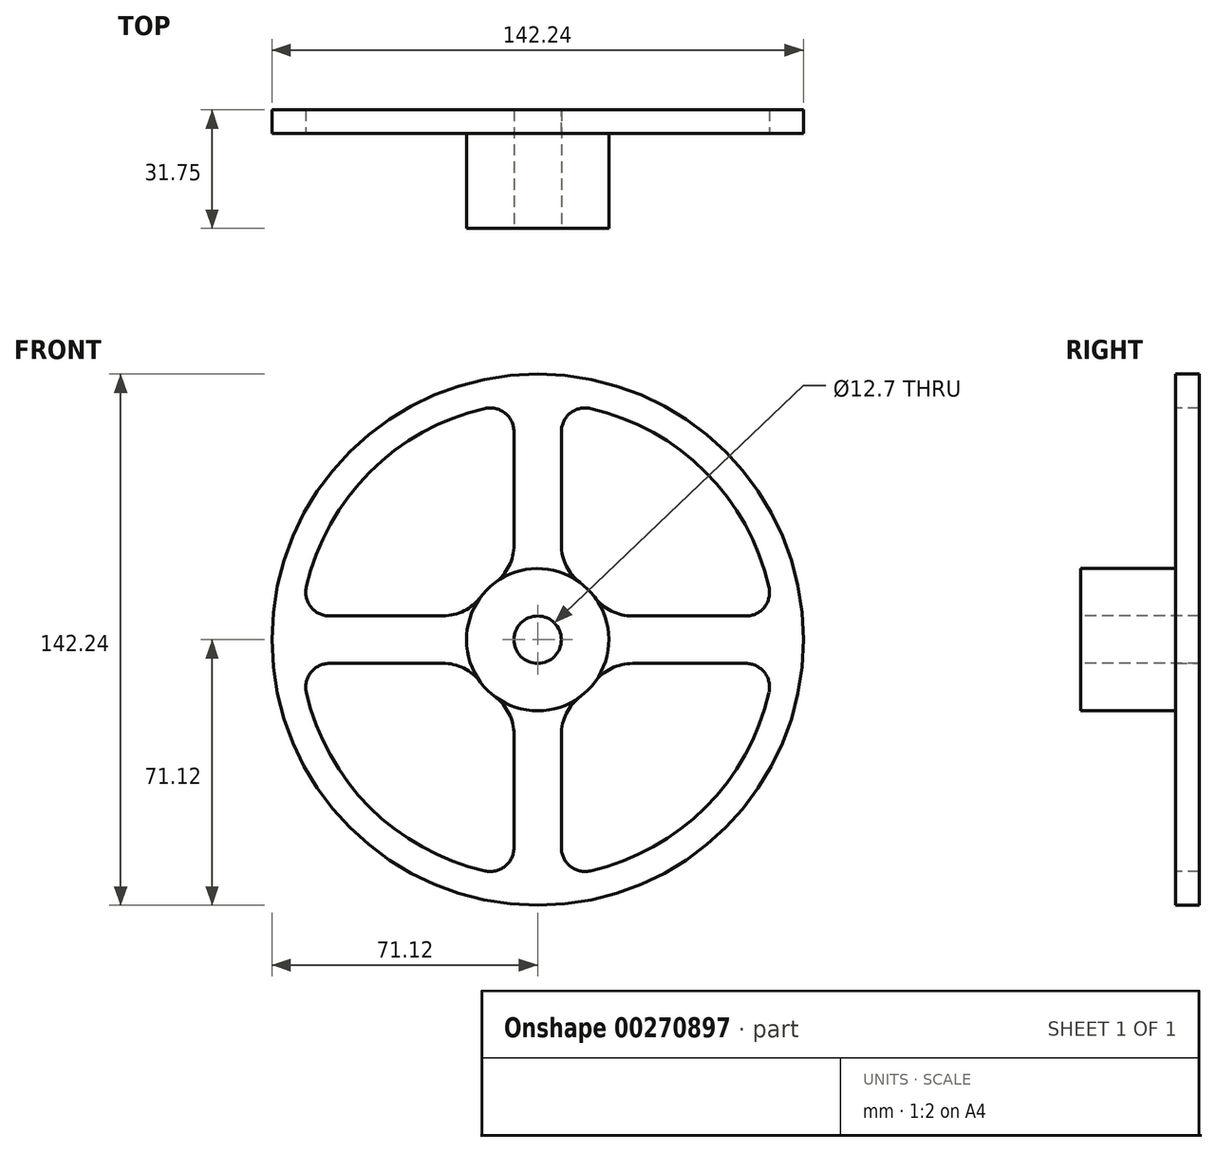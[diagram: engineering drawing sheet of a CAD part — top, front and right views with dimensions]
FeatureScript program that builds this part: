
annotation { "Feature Type Name" : "Feature", "Feature Type Description" : "" }
export const myFeature = defineFeature(function(context is Context, id is Id, definition is map)
    precondition{}
    {
        {
            var Q0;
            Q0=qCreatedBy(makeId("Front.planeOp"),FACE);
            var sketch = newSketch(context, id + "F0", { "sketchPlane" : qUnion([Q0])});
            skCircle(sketch, "E0", {"center": v(0, 0) * mm, "radius": 71.12 * mm});
            skSolve(sketch);
        }
        {
            var Q0;
            Q0=makeQuery(id+"F0.imprint","IMPRINT",FACE,{"disambiguationData":[TD([[makeQuery(id+"F0.imprint","IMPRINT",EDGE,{"derivedFrom":sQuery(id+"F0.wireOp",EDGE,"E0")}),1.0]])]});
            extrude(context, id + "F1", {"entities" : qUnion([Q0]), "depth" : 6.35 * mm});
        }
        {
            var Q0;
            Q0=makeQuery(id+"F1.opExtrude","CAP_FACE",FACE,{"disambiguationData":[OSD([sQuery(id+"F0.wireOp",EDGE,"E0")])],"isStart":false});
            var sketch = newSketch(context, id + "F2", { "sketchPlane" : qUnion([Q0])});
            skCircle(sketch, "E1", {"center": v(0, 0) * mm, "radius": 19.05 * mm});
            skSolve(sketch);
        }
        {
            var Q0;
            Q0=makeQuery(id+"F2.imprint","IMPRINT",FACE,{"disambiguationData":[TD([[makeQuery(id+"F2.imprint","IMPRINT",EDGE,{"derivedFrom":sQuery(id+"F2.wireOp",EDGE,"E1")}),1.0]])]});
            extrude(context, id + "F3", {"entities" : qUnion([Q0]), "operationType" : NewBodyOperationType.ADD, "depth" : 25.4 * mm});
        }
        {
            var Q0;
            Q0=makeQuery(id+"F1.opExtrude","CAP_FACE",FACE,{"disambiguationData":[OSD([sQuery(id+"F0.wireOp",EDGE,"E0")])],"isStart":false});
            var sketch = newSketch(context, id + "F4", { "sketchPlane" : qUnion([Q0])});
            skArc(sketch, "E2", {"start": v(-14.11, 61.91) * mm, "mid": v(-44.9, 44.9) * mm, "end": v(-61.9, 14.12) * mm});
            skLineSegment(sketch, "E3.0", {"start": v(6.35, 17.96) * mm, "end": v(6.35, 55.72) * mm});
            skLineSegment(sketch, "E3.1", {"start": v(17.96, 6.35) * mm, "end": v(55.72, 6.35) * mm});
            skLineSegment(sketch, "E4.0", {"start": v(-6.35, 17.96) * mm, "end": v(-6.35, 55.72) * mm});
            skCircle(sketch, "E5.0.0", {"center": v(0, 0) * mm, "radius": 71.12 * mm});
            skCircle(sketch, "E6.0", {"center": v(0, 0) * mm, "radius": 19.05 * mm});
            skLineSegment(sketch, "E7.trimOffspring", {"start": v(6.35, -17.96) * mm, "end": v(6.35, -55.72) * mm});
            skLineSegment(sketch, "E8.trimOffspring", {"start": v(17.96, -6.35) * mm, "end": v(55.72, -6.35) * mm});
            skLineSegment(sketch, "E9.trimOffspring", {"start": v(-6.35, -17.96) * mm, "end": v(-6.35, -55.72) * mm, "construction": true});
            skLineSegment(sketch, "E10.trimOffspring", {"start": v(-6.35, -17.96) * mm, "end": v(-6.35, -55.72) * mm});
            skPoint(sketch, "E11.visualSharp", {"position": v(-6.35, 63.18) * mm});
            skArc(sketch, "E11.filletArc", {"start": v(-6.35, 55.72) * mm, "mid": v(-8.74, 60.69) * mm, "end": v(-14.11, 61.91) * mm});
            skPoint(sketch, "E12.visualSharp", {"position": v(6.35, 63.18) * mm});
            skArc(sketch, "E12.filletArc", {"start": v(14.11, 61.91) * mm, "mid": v(8.74, 60.69) * mm, "end": v(6.35, 55.72) * mm});
            skLineSegment(sketch, "E13.0", {"start": v(-17.93, 6.42) * mm, "end": v(-55.7, 6.36) * mm});
            skLineSegment(sketch, "E14.0", {"start": v(-17.99, -6.28) * mm, "end": v(-55.73, -6.34) * mm});
            skArc(sketch, "E15.trimOffspring", {"start": v(-61.92, -14.1) * mm, "mid": v(-44.9, -44.9) * mm, "end": v(-14.11, -61.91) * mm});
            skPoint(sketch, "E16.visualSharp", {"position": v(-63.18, 6.35) * mm});
            skArc(sketch, "E16.filletArc", {"start": v(-61.9, 14.12) * mm, "mid": v(-60.68, 8.75) * mm, "end": v(-55.7, 6.36) * mm});
            skArc(sketch, "E17.trimOffspring", {"start": v(61.91, 14.11) * mm, "mid": v(44.9, 44.9) * mm, "end": v(14.11, 61.91) * mm});
            skPoint(sketch, "E18.visualSharp", {"position": v(63.18, 6.35) * mm});
            skArc(sketch, "E18.filletArc", {"start": v(55.72, 6.35) * mm, "mid": v(60.69, 8.74) * mm, "end": v(61.91, 14.11) * mm});
            skPoint(sketch, "E19.visualSharp", {"position": v(63.18, -6.35) * mm});
            skArc(sketch, "E19.filletArc", {"start": v(61.91, -14.11) * mm, "mid": v(60.69, -8.74) * mm, "end": v(55.72, -6.35) * mm});
            skArc(sketch, "E20.trimOffspring", {"start": v(14.11, -61.91) * mm, "mid": v(44.9, -44.9) * mm, "end": v(61.91, -14.11) * mm});
            skPoint(sketch, "E21.visualSharp", {"position": v(-6.35, -63.18) * mm});
            skArc(sketch, "E21.filletArc", {"start": v(-14.11, -61.91) * mm, "mid": v(-8.74, -60.69) * mm, "end": v(-6.35, -55.72) * mm});
            skPoint(sketch, "E22.visualSharp", {"position": v(6.35, -63.18) * mm});
            skArc(sketch, "E22.filletArc", {"start": v(6.35, -55.72) * mm, "mid": v(8.74, -60.69) * mm, "end": v(14.11, -61.91) * mm});
            skPoint(sketch, "E23.visualSharp", {"position": v(-63.18, -6.35) * mm});
            skArc(sketch, "E23.filletArc", {"start": v(-55.73, -6.34) * mm, "mid": v(-60.7, -8.73) * mm, "end": v(-61.92, -14.1) * mm});
            skSolve(sketch);
        }
        {
            var Q0;
            Q0=makeQuery(id+"F4.imprint","IMPRINT",FACE,{"disambiguationData":[TD([[makeQuery(id+"F4.imprint","IMPRINT",EDGE,{"derivedFrom":sQuery(id+"F4.wireOp",EDGE,"E2")}),1.0]])]});
            var Q1;
            {var subQ1=sQuery(id+"F4.wireOp",EDGE,"E3.0");Q1=makeQuery(id+"F4.imprint","IMPRINT",FACE,{"disambiguationData":[TD([[makeQuery(id+"F4.imprint","IMPRINT",EDGE,{"derivedFrom":subQ1}),-1.0]])]});}
            var Q2;
            {var subQ0=sQuery(id+"F4.wireOp",EDGE,"E7.trimOffspring");Q2=makeQuery(id+"F4.imprint","IMPRINT",FACE,{"disambiguationData":[TD([[makeQuery(id+"F4.imprint","IMPRINT",EDGE,{"derivedFrom":subQ0}),1.0]])]});}
            var Q3;
            {var subQ0=sQuery(id+"F4.wireOp",EDGE,"E10.trimOffspring");Q3=makeQuery(id+"F4.imprint","IMPRINT",FACE,{"disambiguationData":[TD([[makeQuery(id+"F4.imprint","IMPRINT",EDGE,{"derivedFrom":subQ0}),-1.0]])]});}
            extrude(context, id + "F5", {"entities" : qUnion([Q0, Q1, Q2, Q3]), "operationType" : NewBodyOperationType.REMOVE, "oppositeDirection" : true, "depth" : 25.4 * mm});
        }
        {
            var Q0;
            Q0=makeQuery(id+"F3.opExtrude","CAP_FACE",FACE,{"disambiguationData":[OSD([sQuery(id+"F2.wireOp",EDGE,"E1")])],"isStart":false});
            var sketch = newSketch(context, id + "F6", { "sketchPlane" : qUnion([Q0])});
            skCircle(sketch, "E24", {"center": v(0, 0) * mm, "radius": 6.35 * mm});
            skSolve(sketch);
        }
        {
            var Q0;
            Q0 = qSketchRegion(id + "F6", true);
            extrude(context, id + "F7", {"entities" : qUnion([Q0]), "operationType" : NewBodyOperationType.REMOVE, "oppositeDirection" : true, "depth" : 31.75 * mm});
        }
        {
            var Q0;
            Q0=makeQuery(id+"F5.boolean.opBoolean","COPY",EDGE,{"derivedFrom":makeQuery(id+"F5.opExtrude","SWEPT_EDGE",EDGE,{"disambiguationData":[OSD([sQuery(id+"F4.wireOp",EDGE,"E6.0"),sQuery(id+"F4.wireOp",EDGE,"E13.0")])]})});
            var Q1;
            Q1=makeQuery(id+"F5.boolean.opBoolean","COPY",EDGE,{"derivedFrom":makeQuery(id+"F5.opExtrude","SWEPT_EDGE",EDGE,{"disambiguationData":[OSD([sQuery(id+"F4.wireOp",EDGE,"E6.0"),sQuery(id+"F4.wireOp",EDGE,"E14.0")])]})});
            var Q2;
            Q2=makeQuery(id+"F5.boolean.opBoolean","COPY",EDGE,{"derivedFrom":makeQuery(id+"F5.opExtrude","SWEPT_EDGE",EDGE,{"disambiguationData":[OSD([sQuery(id+"F4.wireOp",EDGE,"E6.0"),sQuery(id+"F4.wireOp",EDGE,"E7.trimOffspring")])]})});
            var Q3;
            Q3=makeQuery(id+"F5.boolean.opBoolean","COPY",EDGE,{"derivedFrom":makeQuery(id+"F5.opExtrude","SWEPT_EDGE",EDGE,{"disambiguationData":[OSD([sQuery(id+"F4.wireOp",EDGE,"E6.0"),sQuery(id+"F4.wireOp",EDGE,"E8.trimOffspring")])]})});
            var Q4;
            Q4=makeQuery(id+"F5.boolean.opBoolean","COPY",EDGE,{"derivedFrom":makeQuery(id+"F5.opExtrude","SWEPT_EDGE",EDGE,{"disambiguationData":[OSD([sQuery(id+"F4.wireOp",EDGE,"E3.1"),sQuery(id+"F4.wireOp",EDGE,"E6.0")])]})});
            var Q5;
            Q5=makeQuery(id+"F5.boolean.opBoolean","COPY",EDGE,{"derivedFrom":makeQuery(id+"F5.opExtrude","SWEPT_EDGE",EDGE,{"disambiguationData":[OSD([sQuery(id+"F4.wireOp",EDGE,"E3.0"),sQuery(id+"F4.wireOp",EDGE,"E6.0")])]})});
            var Q6;
            Q6=makeQuery(id+"F5.boolean.opBoolean","COPY",EDGE,{"derivedFrom":makeQuery(id+"F5.opExtrude","SWEPT_EDGE",EDGE,{"disambiguationData":[OSD([sQuery(id+"F4.wireOp",EDGE,"E4.0"),sQuery(id+"F4.wireOp",EDGE,"E6.0")])]})});
            var Q7;
            Q7=makeQuery(id+"F5.boolean.opBoolean","COPY",EDGE,{"derivedFrom":makeQuery(id+"F5.opExtrude","SWEPT_EDGE",EDGE,{"disambiguationData":[OSD([sQuery(id+"F4.wireOp",EDGE,"E6.0"),sQuery(id+"F4.wireOp",EDGE,"E10.trimOffspring")])]})});
            fillet(context, id + "F8", {"entities" : qUnion([Q0, Q1, Q2, Q3, Q4, Q5, Q6, Q7]), "radius" : 12.7 * mm, "tangentPropagation" : true, "allowEdgeOverflow" : false});
        }
    });
